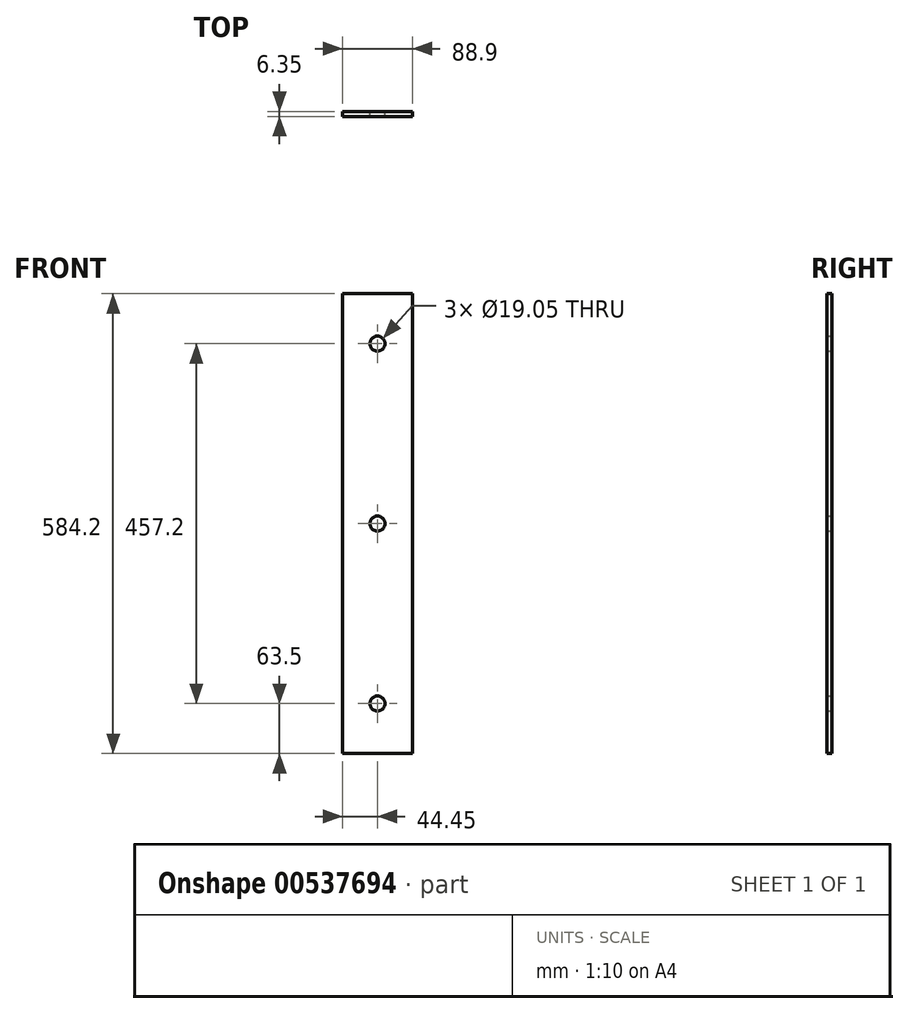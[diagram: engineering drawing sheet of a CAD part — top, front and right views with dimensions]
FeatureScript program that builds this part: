
annotation { "Feature Type Name" : "Feature", "Feature Type Description" : "" }
export const myFeature = defineFeature(function(context is Context, id is Id, definition is map)
    precondition{}
    {
        {
            var Q0;
            Q0=qCreatedBy(makeId("Front.planeOp"),FACE);
            var sketch = newSketch(context, id + "F0", { "sketchPlane" : qUnion([Q0])});
            skLineSegment(sketch, "E0.bottom", {"start": v(44.45, 292.1) * mm, "end": v(-44.45, 292.1) * mm});
            skLineSegment(sketch, "E0.top", {"start": v(44.45, -292.1) * mm, "end": v(-44.45, -292.1) * mm});
            skLineSegment(sketch, "E0.left", {"start": v(44.45, 292.1) * mm, "end": v(44.45, -292.1) * mm});
            skLineSegment(sketch, "E0.right", {"start": v(-44.45, 292.1) * mm, "end": v(-44.45, -292.1) * mm});
            skPoint(sketch, "E0.middle", {"position": v(0, 0) * mm});
            skLineSegment(sketch, "E1", {"start": v(0, -292.1) * mm, "end": v(0, 292.1) * mm, "construction": true});
            skCircle(sketch, "E2", {"center": v(0, 228.6) * mm, "radius": 9.53 * mm});
            skCircle(sketch, "E3", {"center": v(0, 0) * mm, "radius": 9.53 * mm});
            skCircle(sketch, "E4", {"center": v(0, -228.6) * mm, "radius": 9.53 * mm});
            skSolve(sketch);
        }
        {
            var Q0;
            Q0=makeQuery(id+"F0.imprint","IMPRINT",FACE,{"disambiguationData":[TD([[makeQuery(id+"F0.imprint","IMPRINT",EDGE,{"derivedFrom":sQuery(id+"F0.wireOp",EDGE,"E0.bottom")}),1.0]])]});
            extrude(context, id + "F1", {"entities" : qUnion([Q0]), "depth" : 6.35 * mm, "offsetDistance" : 25.4 * mm});
        }
    });
